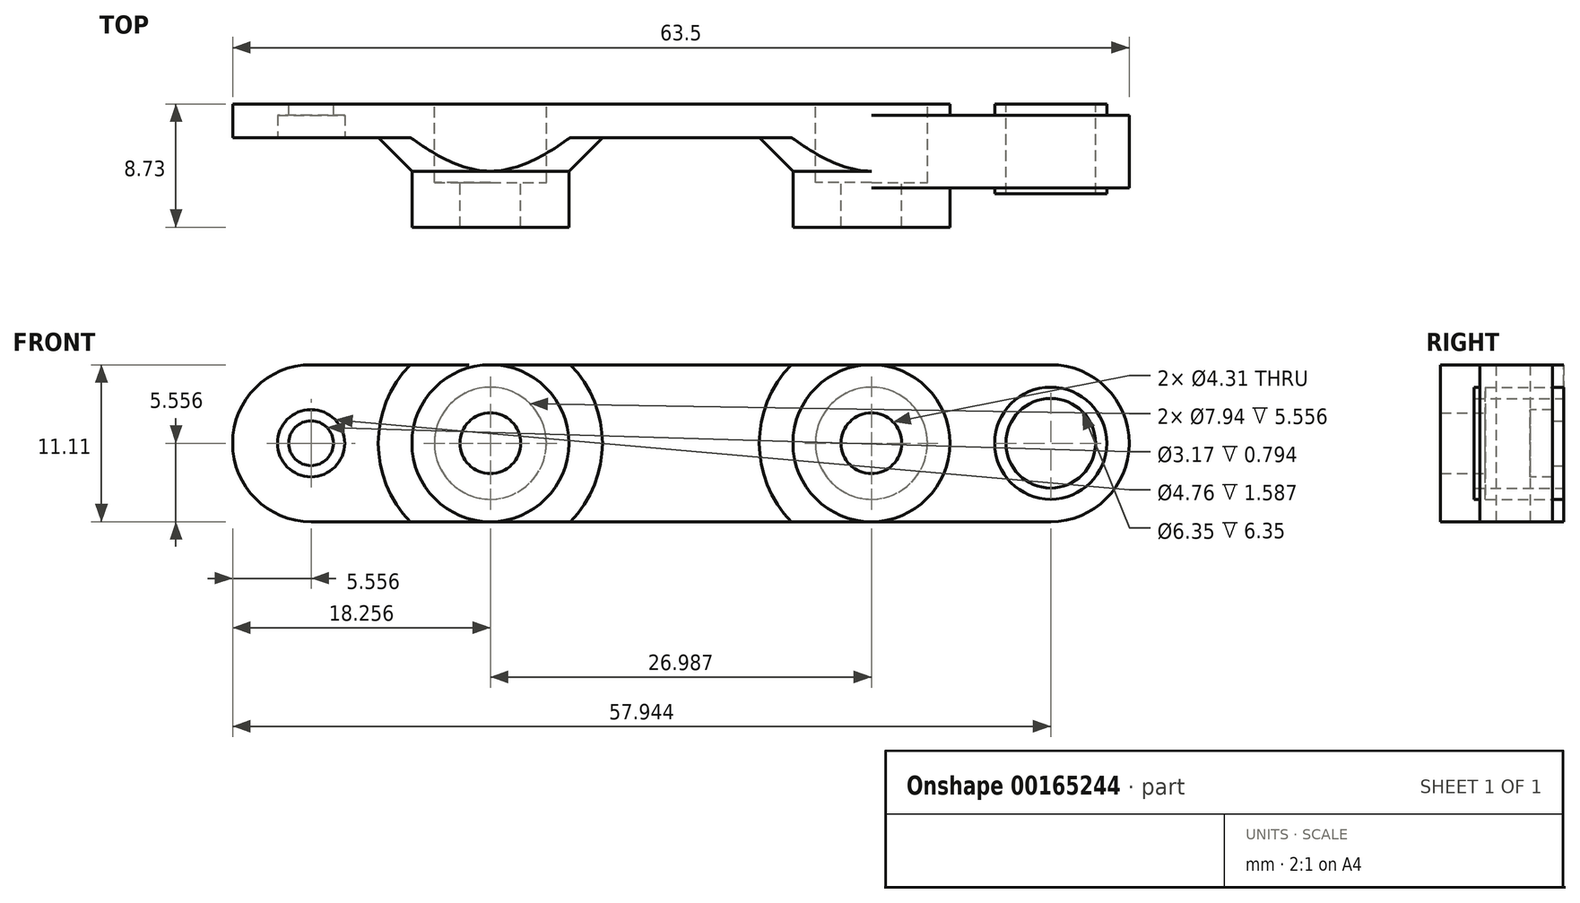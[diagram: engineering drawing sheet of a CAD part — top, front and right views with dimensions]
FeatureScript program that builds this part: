
annotation { "Feature Type Name" : "Feature", "Feature Type Description" : "" }
export const myFeature = defineFeature(function(context is Context, id is Id, definition is map)
    precondition{}
    {
        {
            var Q0;
            Q0=qCreatedBy(makeId("Top.planeOp"),FACE);
            var sketch = newSketch(context, id + "F0", { "sketchPlane" : qUnion([Q0])});
            skLineSegment(sketch, "E0.bottom", {"start": v(0, 0) * mm, "end": v(-12.7, 0) * mm});
            skLineSegment(sketch, "E0.top", {"start": v(38.1, 2.38) * mm, "end": v(-12.7, 2.38) * mm});
            skLineSegment(sketch, "E0.right", {"start": v(-12.7, 0) * mm, "end": v(-12.7, 2.38) * mm});
            skLineSegment(sketch, "E1.left", {"start": v(0, 0) * mm, "end": v(0, -6.35) * mm});
            skLineSegment(sketch, "E1.right", {"start": v(38.1, -3.57) * mm, "end": v(38.1, -6.35) * mm});
            skLineSegment(sketch, "E2", {"start": v(38.1, -3.57) * mm, "end": v(50.8, -3.57) * mm});
            skLineSegment(sketch, "E3", {"start": v(50.8, -3.57) * mm, "end": v(50.8, 1.59) * mm});
            skLineSegment(sketch, "E4", {"start": v(0, -6.35) * mm, "end": v(11.11, -6.35) * mm});
            skLineSegment(sketch, "E5", {"start": v(11.11, -6.35) * mm, "end": v(11.11, 0) * mm});
            skLineSegment(sketch, "E6", {"start": v(11.11, 0) * mm, "end": v(26.99, 0) * mm});
            skLineSegment(sketch, "E7", {"start": v(26.99, 0) * mm, "end": v(26.99, -6.35) * mm});
            skLineSegment(sketch, "E8", {"start": v(26.99, -6.35) * mm, "end": v(38.1, -6.35) * mm});
            skLineSegment(sketch, "E9", {"start": v(38.1, 2.38) * mm, "end": v(38.1, 1.59) * mm});
            skLineSegment(sketch, "E10", {"start": v(38.1, 1.59) * mm, "end": v(50.8, 1.59) * mm});
            skLineSegment(sketch, "E11", {"start": v(38.1, -6.35) * mm, "end": v(38.1, -8.73) * mm, "construction": true});
            skLineSegment(sketch, "E12", {"start": v(38.1, -8.73) * mm, "end": v(50.8, -8.73) * mm, "construction": true});
            skLineSegment(sketch, "E13", {"start": v(50.8, -8.73) * mm, "end": v(50.8, -3.57) * mm, "construction": true});
            skSolve(sketch);
        }
        {
            var Q0;
            Q0=qSketchRegion(id+"F0",true);
            extrude(context, id + "F1", {"entities" : qUnion([Q0]), "depth" : 11.1 * mm});
        }
        {
            var Q0;
            Q0=makeQuery(id+"F1.opExtrude","SWEPT_FACE",FACE,{"disambiguationData":[OSD([sQuery(id+"F0.wireOp",EDGE,"E0.top")])]});
            var sketch = newSketch(context, id + "F2", { "sketchPlane" : qUnion([Q0])});
            skCircle(sketch, "E14", {"center": v(-45.24, 5.56) * mm, "radius": 3.18 * mm});
            skCircle(sketch, "E15", {"center": v(7.14, 5.56) * mm, "radius": 1.59 * mm});
            skLineSegment(sketch, "E16", {"start": v(-32.54, 0) * mm, "end": v(-32.54, 11.11) * mm, "construction": true});
            skLineSegment(sketch, "E17", {"start": v(-5.56, 0) * mm, "end": v(-5.56, 11.11) * mm, "construction": true});
            skCircle(sketch, "E18", {"center": v(-5.56, 5.56) * mm, "radius": 2.15 * mm});
            skCircle(sketch, "E19", {"center": v(-32.54, 5.56) * mm, "radius": 2.15 * mm});
            skLineSegment(sketch, "E20", {"start": v(12.7, 5.56) * mm, "end": v(7.14, 5.56) * mm, "construction": true});
            skLineSegment(sketch, "E21", {"start": v(7.14, 5.56) * mm, "end": v(7.14, 11.11) * mm, "construction": true});
            skLineSegment(sketch, "E22", {"start": v(-45.24, 5.56) * mm, "end": v(-45.24, 11.11) * mm, "construction": true});
            skLineSegment(sketch, "E23", {"start": v(-45.24, 5.56) * mm, "end": v(-50.8, 5.56) * mm, "construction": true});
            skSolve(sketch);
        }
        {
            var Q0;
            Q0=qSketchRegion(id+"F2",true);
            var Q1;
            Q1=makeQuery(id+"F1.opExtrude","SWEPT_FACE",FACE,{"disambiguationData":[OSD([sQuery(id+"F0.wireOp",EDGE,"E8")])]});
            extrude(context, id + "F3", {"entities" : qUnion([Q0]), "operationType" : NewBodyOperationType.REMOVE, "endBound" : BoundingType.UP_TO_SURFACE, "oppositeDirection" : true, "endBoundEntityFace" : qUnion([Q1]), "depth" : 25.4 * mm});
        }
        {
            var Q0;
            Q0=makeQuery(id+"F1.opExtrude","SWEPT_FACE",FACE,{"disambiguationData":[OSD([sQuery(id+"F0.wireOp",EDGE,"E0.bottom")])]});
            var sketch = newSketch(context, id + "F4", { "sketchPlane" : qUnion([Q0])});
            skCircle(sketch, "E24", {"center": v(-7.14, 5.56) * mm, "radius": 2.38 * mm});
            skSolve(sketch);
        }
        {
            var Q0;
            Q0=qSketchRegion(id+"F4",true);
            extrude(context, id + "F5", {"entities" : qUnion([Q0]), "operationType" : NewBodyOperationType.REMOVE, "oppositeDirection" : true, "depth" : 1.59 * mm});
        }
        {
            var Q0;
            Q0=makeQuery(id+"F1.opExtrude","SWEPT_FACE",FACE,{"disambiguationData":[OSD([sQuery(id+"F0.wireOp",EDGE,"E10")])]});
            var sketch = newSketch(context, id + "F6", { "sketchPlane" : qUnion([Q0])});
            skCircle(sketch, "E25", {"center": v(-45.24, 5.56) * mm, "radius": 3.18 * mm});
            skCircle(sketch, "E26", {"center": v(-45.24, 5.56) * mm, "radius": 3.97 * mm});
            skSolve(sketch);
        }
        {
            var Q0;
            Q0=qSketchRegion(id+"F6",true);
            var Q1;
            Q1=makeQuery(id+"F1.opExtrude","SWEPT_FACE",FACE,{"disambiguationData":[OSD([sQuery(id+"F0.wireOp",EDGE,"E0.top")])]});
            extrude(context, id + "F7", {"entities" : qUnion([Q0]), "operationType" : NewBodyOperationType.ADD, "endBoundEntityFace" : qUnion([Q1]), "depth" : 0.8 * mm, "hasSecondDirection" : true, "secondDirectionOppositeDirection" : true, "secondDirectionDepth" : 5.56 * mm});
        }
        {
            var Q0;
            Q0=makeQuery(id+"F1.opExtrude","CAP_EDGE",EDGE,{"disambiguationData":[OSD([sQuery(id+"F0.wireOp",EDGE,"E1.left")])],"isStart":true});
            var Q1;
            Q1=makeQuery(id+"F1.opExtrude","CAP_EDGE",EDGE,{"disambiguationData":[OSD([sQuery(id+"F0.wireOp",EDGE,"E1.left")])],"isStart":false});
            var Q2;
            Q2=makeQuery(id+"F1.opExtrude","CAP_EDGE",EDGE,{"disambiguationData":[OSD([sQuery(id+"F0.wireOp",EDGE,"E1.right")])],"isStart":true});
            var Q3;
            Q3=makeQuery(id+"F1.opExtrude","CAP_EDGE",EDGE,{"disambiguationData":[OSD([sQuery(id+"F0.wireOp",EDGE,"E1.right")])],"isStart":false});
            var Q4;
            Q4=makeQuery(id+"F1.opExtrude","CAP_EDGE",EDGE,{"disambiguationData":[OSD([sQuery(id+"F0.wireOp",EDGE,"E9")])],"isStart":true});
            var Q5;
            Q5=makeQuery(id+"F1.opExtrude","CAP_EDGE",EDGE,{"disambiguationData":[OSD([sQuery(id+"F0.wireOp",EDGE,"E9")])],"isStart":false});
            var Q6;
            Q6=makeQuery(id+"F1.opExtrude","CAP_EDGE",EDGE,{"disambiguationData":[OSD([sQuery(id+"F0.wireOp",EDGE,"E5")])],"isStart":false});
            var Q7;
            Q7=makeQuery(id+"F1.opExtrude","CAP_EDGE",EDGE,{"disambiguationData":[OSD([sQuery(id+"F0.wireOp",EDGE,"E5")])],"isStart":true});
            var Q8;
            Q8=makeQuery(id+"F1.opExtrude","CAP_EDGE",EDGE,{"disambiguationData":[OSD([sQuery(id+"F0.wireOp",EDGE,"E7")])],"isStart":false});
            var Q9;
            Q9=makeQuery(id+"F1.opExtrude","CAP_EDGE",EDGE,{"disambiguationData":[OSD([sQuery(id+"F0.wireOp",EDGE,"E7")])],"isStart":true});
            var Q10;
            Q10=makeQuery(id+"F1.opExtrude","CAP_EDGE",EDGE,{"disambiguationData":[OSD([sQuery(id+"F0.wireOp",EDGE,"E3")])],"isStart":false});
            var Q11;
            Q11=makeQuery(id+"F1.opExtrude","CAP_EDGE",EDGE,{"disambiguationData":[OSD([sQuery(id+"F0.wireOp",EDGE,"E3")])],"isStart":true});
            var Q12;
            Q12=makeQuery(id+"F1.opExtrude","CAP_EDGE",EDGE,{"disambiguationData":[OSD([sQuery(id+"F0.wireOp",EDGE,"E0.right")])],"isStart":false});
            var Q13;
            Q13=makeQuery(id+"F1.opExtrude","CAP_EDGE",EDGE,{"disambiguationData":[OSD([sQuery(id+"F0.wireOp",EDGE,"E0.right")])],"isStart":true});
            fillet(context, id + "F8", {"entities" : qUnion([Q0, Q1, Q2, Q3, Q4, Q5, Q6, Q7, Q8, Q9, Q10, Q11, Q12, Q13]), "radius" : 5.56 * mm, "tangentPropagation" : true, "allowEdgeOverflow" : false});
        }
        {
            var Q0;
            Q0=makeQuery(id+"F1.opExtrude","SWEPT_FACE",FACE,{"disambiguationData":[OSD([sQuery(id+"F0.wireOp",EDGE,"E4")])]});
            cPlane(context, id + "F9", {"entities" : qUnion([Q0]), "cplaneType" : CPlaneType.OFFSET, "offset" : 3.17 * mm, "oppositeDirection" : true, "width" : 152.4 * mm, "height" : 152.4 * mm});
        }
        {
            var Q0;
            Q0=makeQuery(id+"F1.opExtrude","SWEPT_FACE",FACE,{"disambiguationData":[OSD([sQuery(id+"F0.wireOp",EDGE,"E0.top")])]});
            var sketch = newSketch(context, id + "F10", { "sketchPlane" : qUnion([Q0])});
            skCircle(sketch, "E27", {"center": v(-32.54, 5.56) * mm, "radius": 3.97 * mm});
            skCircle(sketch, "E28", {"center": v(-5.56, 5.56) * mm, "radius": 3.97 * mm});
            skSolve(sketch);
        }
        {
            var Q0;
            Q0=qSketchRegion(id+"F10",true);
            var Q1;
            Q1=qCreatedBy(id+"F9.planeOp",FACE);
            extrude(context, id + "F11", {"entities" : qUnion([Q0]), "operationType" : NewBodyOperationType.REMOVE, "endBound" : BoundingType.UP_TO_SURFACE, "oppositeDirection" : true, "endBoundEntityFace" : qUnion([Q1]), "depth" : 25.4 * mm});
        }
        {
            var Q0;
            Q0=makeQuery(id+"F8.opFillet","BLEND_EDGE",EDGE,{"blendedFrom":[makeQuery(id+"F1.opExtrude","CAP_EDGE",EDGE,{"disambiguationData":[OSD([sQuery(id+"F0.wireOp",EDGE,"E5")])],"isStart":true}),makeQuery(id+"F1.opExtrude","SWEPT_FACE",FACE,{"disambiguationData":[OSD([sQuery(id+"F0.wireOp",EDGE,"E6")])]})],"blendedInto":[makeQuery(id+"F1.opExtrude","SWEPT_FACE",FACE,{"disambiguationData":[OSD([sQuery(id+"F0.wireOp",EDGE,"E6")])]})]});
            var Q1;
            Q1=makeQuery(id+"F8.opFillet","BLEND_EDGE",EDGE,{"blendedFrom":[makeQuery(id+"F1.opExtrude","CAP_EDGE",EDGE,{"disambiguationData":[OSD([sQuery(id+"F0.wireOp",EDGE,"E7")])],"isStart":true}),makeQuery(id+"F1.opExtrude","SWEPT_FACE",FACE,{"disambiguationData":[OSD([sQuery(id+"F0.wireOp",EDGE,"E6")])]})],"blendedInto":[makeQuery(id+"F1.opExtrude","SWEPT_FACE",FACE,{"disambiguationData":[OSD([sQuery(id+"F0.wireOp",EDGE,"E6")])]})]});
            chamfer(context, id + "F12", {"entities" : qUnion([Q0, Q1]), "width" : 2.38 * mm, "tangentPropagation" : true});
        }
    });
